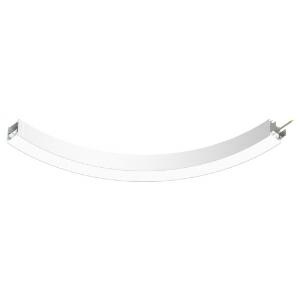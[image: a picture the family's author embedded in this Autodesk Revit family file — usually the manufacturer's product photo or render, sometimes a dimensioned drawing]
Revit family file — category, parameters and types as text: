
# Revit family: super-g_slim_super_g_slim_1550_90deg_ab_ps_led__24w_3160lm_3000k_cri_80_350-1400_1b16
name_source: partatom
category: Leuchten
revit_build: Autodesk Revit 2016 (Build: 20190508_0715(x64)
units: mm (PartAtom-declared; Revit-internal decimal feet)

## family parameters
Basisbauteil = Fläche
Beim Laden mit Abzugskörper schneiden = Nein
Bemaßung runder Anschluss = Durchmesser verwenden
Gemeinsam genutzt = Nein
Lichtquelle = Nein
Raumberechnungspunkt = Nein
Teiletyp = Normal

## types (1)
- 350-1400-D01 (1 x LED, 480 lm, 3000K)
    Approval mark = CE
    Beschreibung = The insert consists of aluminum-extruded profile. Charming SOFT-EDGE design ensure unparalleled styling. The ballast is integrated and allows for an operation with 220-240V (50/60Hz). SUPER-G SLIM (# 350-1400) ist not dimmable (on/off).
    CIE Flux Codes = 48 79 96 100 71
    Color Rendering = 1B/80…89
    Color Temperature = 3000K
    Height = 90 mm
    Hersteller = Prolicht
    Lamp Light Flux = 480 lm
    Lamp count = 1
    Lampe = 1 x LED
    Length = 146 mm
    Luminous efficacy = 103 lm/W
    ModVariant = Nein
    Modell = 350-1400
    Mounting Place = Ceiling
    Mounting Type = Surface mounted
    Number of Poles = 1
    OnlyDefault = Ja
    Power Factor = 1
    Product Name = SUPER-G SLIM__SUPER G SLIM 1550/90° AB PS LED: 24W 3160lm 3000K CRI:80
    Product group = Surface profile systems
    ProductGroupID = 335
    Protection Class = Protection class I
    Protection Degree = IP 20
    RLX_Detail_Level = 1
    RlxData = <blob elided: 38573 chars, md5=005a0ed7>
    Scheinlast = 26 VA
    Socket = socket
    Standby Power = 0 W
    System Light Flux = 2723 lm
    System Power = 26 W
    Typenbild = 350-1400.jpg
    URL = http://relux.com
    VarID = 350-1400-d01
    Voltage = 0 V
    Vorgabe-Ansicht = 1800 mm
    Weight = 0.00 kg
    Width = 65 mm

## geometry (parser evidence)
native form markers: Sweep x29
no freeform markers — native parametric forms only
